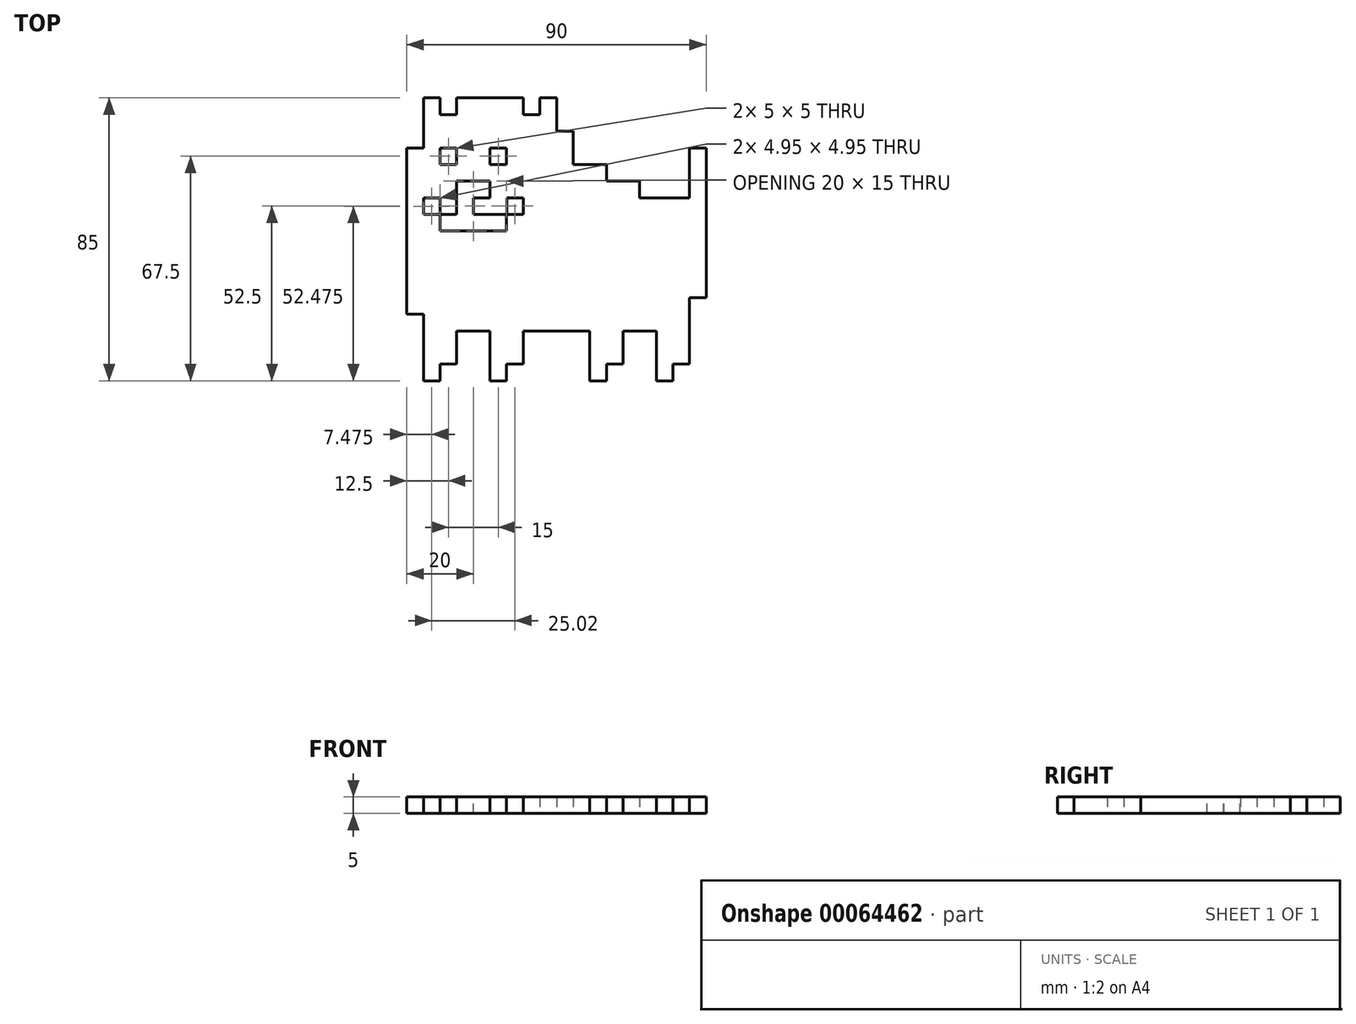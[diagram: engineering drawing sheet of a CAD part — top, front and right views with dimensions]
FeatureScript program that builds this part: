
annotation { "Feature Type Name" : "Feature", "Feature Type Description" : "" }
export const myFeature = defineFeature(function(context is Context, id is Id, definition is map)
    precondition{}
    {
        {
            var Q0;
            Q0=qCreatedBy(makeId("Top.planeOp"),FACE);
            var sketch = newSketch(context, id + "F0", { "sketchPlane" : qUnion([Q0])});
            skPoint(sketch, "E0", {"position": v(0, 25) * mm});
            skPoint(sketch, "E1", {"position": v(0, -25) * mm});
            skLineSegment(sketch, "E2", {"start": v(0, 25) * mm, "end": v(0, -25) * mm});
            skLineSegment(sketch, "E3", {"start": v(0, 25) * mm, "end": v(5, 25) * mm});
            skLineSegment(sketch, "E4", {"start": v(5, 25) * mm, "end": v(5, 40) * mm});
            skLineSegment(sketch, "E5", {"start": v(5, 40) * mm, "end": v(10, 40) * mm});
            skLineSegment(sketch, "E6", {"start": v(10, 40) * mm, "end": v(10, 35) * mm});
            skLineSegment(sketch, "E7", {"start": v(10, 35) * mm, "end": v(15, 35) * mm});
            skLineSegment(sketch, "E8", {"start": v(15, 35) * mm, "end": v(15, 40) * mm});
            skLineSegment(sketch, "E9", {"start": v(15, 40) * mm, "end": v(35, 40) * mm});
            skLineSegment(sketch, "E10", {"start": v(35, 40) * mm, "end": v(35, 35) * mm});
            skLineSegment(sketch, "E11", {"start": v(35, 35) * mm, "end": v(40, 35) * mm});
            skLineSegment(sketch, "E12", {"start": v(40, 35) * mm, "end": v(40, 40) * mm});
            skLineSegment(sketch, "E13", {"start": v(40, 40) * mm, "end": v(45, 40) * mm});
            skLineSegment(sketch, "E14", {"start": v(45, 40) * mm, "end": v(45, 30) * mm});
            skLineSegment(sketch, "E15", {"start": v(45, 30) * mm, "end": v(50, 30) * mm});
            skLineSegment(sketch, "E16", {"start": v(50, 30) * mm, "end": v(50, 20) * mm});
            skLineSegment(sketch, "E17", {"start": v(50, 20) * mm, "end": v(60, 20) * mm});
            skLineSegment(sketch, "E18", {"start": v(60, 20) * mm, "end": v(60, 15) * mm});
            skLineSegment(sketch, "E19", {"start": v(60, 15) * mm, "end": v(70, 15) * mm});
            skLineSegment(sketch, "E20", {"start": v(70, 15) * mm, "end": v(70, 10) * mm});
            skLineSegment(sketch, "E21", {"start": v(70, 10) * mm, "end": v(85, 10) * mm});
            skLineSegment(sketch, "E22", {"start": v(85, 10) * mm, "end": v(85, 25) * mm});
            skLineSegment(sketch, "E23", {"start": v(85, 25) * mm, "end": v(90, 25) * mm});
            skLineSegment(sketch, "E24", {"start": v(90, 25) * mm, "end": v(90, -20) * mm});
            skLineSegment(sketch, "E25", {"start": v(90, -20) * mm, "end": v(85, -20) * mm});
            skLineSegment(sketch, "E26", {"start": v(85, -20) * mm, "end": v(85, -40) * mm});
            skLineSegment(sketch, "E27", {"start": v(85, -40) * mm, "end": v(80, -40) * mm});
            skLineSegment(sketch, "E28", {"start": v(80, -40) * mm, "end": v(80, -45) * mm});
            skLineSegment(sketch, "E29", {"start": v(80, -45) * mm, "end": v(75, -45) * mm});
            skLineSegment(sketch, "E30", {"start": v(75, -45) * mm, "end": v(75, -30) * mm});
            skLineSegment(sketch, "E31", {"start": v(75, -30) * mm, "end": v(65, -30) * mm});
            skLineSegment(sketch, "E32", {"start": v(65, -30) * mm, "end": v(65, -40) * mm});
            skLineSegment(sketch, "E33", {"start": v(65, -40) * mm, "end": v(60, -40) * mm});
            skLineSegment(sketch, "E34", {"start": v(60, -40) * mm, "end": v(60, -45) * mm});
            skLineSegment(sketch, "E35", {"start": v(60, -45) * mm, "end": v(55, -45) * mm});
            skLineSegment(sketch, "E36", {"start": v(55, -45) * mm, "end": v(55, -30) * mm});
            skLineSegment(sketch, "E37", {"start": v(55, -30) * mm, "end": v(35, -30) * mm});
            skLineSegment(sketch, "E38", {"start": v(35, -30) * mm, "end": v(35, -40) * mm});
            skLineSegment(sketch, "E39", {"start": v(35, -40) * mm, "end": v(30, -40) * mm});
            skLineSegment(sketch, "E40", {"start": v(30, -40) * mm, "end": v(30, -45) * mm});
            skLineSegment(sketch, "E41", {"start": v(30, -45) * mm, "end": v(25, -45) * mm});
            skLineSegment(sketch, "E42", {"start": v(25, -45) * mm, "end": v(25, -30) * mm});
            skLineSegment(sketch, "E43", {"start": v(25, -30) * mm, "end": v(15, -30) * mm});
            skLineSegment(sketch, "E44", {"start": v(15, -30) * mm, "end": v(15, -40) * mm});
            skLineSegment(sketch, "E45", {"start": v(15, -40) * mm, "end": v(10, -40) * mm});
            skLineSegment(sketch, "E46", {"start": v(10, -40) * mm, "end": v(10, -45) * mm});
            skLineSegment(sketch, "E47", {"start": v(10, -45) * mm, "end": v(5, -45) * mm});
            skLineSegment(sketch, "E48", {"start": v(0, -25) * mm, "end": v(5, -25) * mm});
            skLineSegment(sketch, "E49", {"start": v(5, -45) * mm, "end": v(5, -25) * mm});
            skSolve(sketch);
        }
        {
            var Q0;
            Q0 = qSketchRegion(id + "F0", true);
            extrude(context, id + "F1", {"entities" : qUnion([Q0]), "depth" : 5 * mm});
        }
        {
            var Q0;
            Q0=makeQuery(id+"F1.opExtrude","CAP_FACE",FACE,{"disambiguationData":[OSD([sQuery(id+"F0.wireOp",EDGE,"E2"),sQuery(id+"F0.wireOp",EDGE,"E3"),sQuery(id+"F0.wireOp",EDGE,"E4"),sQuery(id+"F0.wireOp",EDGE,"E5"),sQuery(id+"F0.wireOp",EDGE,"E6"),sQuery(id+"F0.wireOp",EDGE,"E7"),sQuery(id+"F0.wireOp",EDGE,"E8"),sQuery(id+"F0.wireOp",EDGE,"E9"),sQuery(id+"F0.wireOp",EDGE,"E10"),sQuery(id+"F0.wireOp",EDGE,"E11"),sQuery(id+"F0.wireOp",EDGE,"E12"),sQuery(id+"F0.wireOp",EDGE,"E13"),sQuery(id+"F0.wireOp",EDGE,"E14"),sQuery(id+"F0.wireOp",EDGE,"E15"),sQuery(id+"F0.wireOp",EDGE,"E16"),sQuery(id+"F0.wireOp",EDGE,"E17"),sQuery(id+"F0.wireOp",EDGE,"E18"),sQuery(id+"F0.wireOp",EDGE,"E19"),sQuery(id+"F0.wireOp",EDGE,"E20"),sQuery(id+"F0.wireOp",EDGE,"E21"),sQuery(id+"F0.wireOp",EDGE,"E22"),sQuery(id+"F0.wireOp",EDGE,"E23"),sQuery(id+"F0.wireOp",EDGE,"E24"),sQuery(id+"F0.wireOp",EDGE,"E25"),sQuery(id+"F0.wireOp",EDGE,"E26"),sQuery(id+"F0.wireOp",EDGE,"E27"),sQuery(id+"F0.wireOp",EDGE,"E28"),sQuery(id+"F0.wireOp",EDGE,"E29"),sQuery(id+"F0.wireOp",EDGE,"E30"),sQuery(id+"F0.wireOp",EDGE,"E31"),sQuery(id+"F0.wireOp",EDGE,"E32"),sQuery(id+"F0.wireOp",EDGE,"E33"),sQuery(id+"F0.wireOp",EDGE,"E34"),sQuery(id+"F0.wireOp",EDGE,"E35"),sQuery(id+"F0.wireOp",EDGE,"E36"),sQuery(id+"F0.wireOp",EDGE,"E37"),sQuery(id+"F0.wireOp",EDGE,"E38"),sQuery(id+"F0.wireOp",EDGE,"E39"),sQuery(id+"F0.wireOp",EDGE,"E40"),sQuery(id+"F0.wireOp",EDGE,"E41"),sQuery(id+"F0.wireOp",EDGE,"E42"),sQuery(id+"F0.wireOp",EDGE,"E43"),sQuery(id+"F0.wireOp",EDGE,"E44"),sQuery(id+"F0.wireOp",EDGE,"E45"),sQuery(id+"F0.wireOp",EDGE,"E46"),sQuery(id+"F0.wireOp",EDGE,"E47"),sQuery(id+"F0.wireOp",EDGE,"E48"),sQuery(id+"F0.wireOp",EDGE,"E49")])],"isStart":false});
            var sketch = newSketch(context, id + "F2", { "sketchPlane" : qUnion([Q0])});
            skLineSegment(sketch, "E50.bottom", {"start": v(10, 25) * mm, "end": v(15, 25) * mm});
            skLineSegment(sketch, "E50.top", {"start": v(10, 20) * mm, "end": v(15, 20) * mm});
            skLineSegment(sketch, "E50.left", {"start": v(10, 25) * mm, "end": v(10, 20) * mm});
            skLineSegment(sketch, "E50.right", {"start": v(15, 25) * mm, "end": v(15, 20) * mm});
            skLineSegment(sketch, "E51.right", {"start": v(30, 25) * mm, "end": v(30, 20) * mm});
            skLineSegment(sketch, "E51.left", {"start": v(25, 25) * mm, "end": v(25, 20) * mm});
            skLineSegment(sketch, "E51.top", {"start": v(25, 20) * mm, "end": v(30, 20) * mm});
            skLineSegment(sketch, "E51.bottom", {"start": v(25, 25) * mm, "end": v(30, 25) * mm});
            skLineSegment(sketch, "E52.right", {"start": v(10, 10) * mm, "end": v(10, 5) * mm});
            skLineSegment(sketch, "E52.left", {"start": v(5, 10) * mm, "end": v(5, 5) * mm});
            skLineSegment(sketch, "E52.top", {"start": v(5, 5) * mm, "end": v(10, 5) * mm});
            skLineSegment(sketch, "E52.bottom", {"start": v(5, 10) * mm, "end": v(10, 10) * mm});
            skLineSegment(sketch, "E53.right", {"start": v(35, 10) * mm, "end": v(35, 5) * mm});
            skLineSegment(sketch, "E53.left", {"start": v(30, 10) * mm, "end": v(30, 5) * mm});
            skLineSegment(sketch, "E53.top", {"start": v(30, 5) * mm, "end": v(35, 5) * mm});
            skLineSegment(sketch, "E53.bottom", {"start": v(30, 10) * mm, "end": v(35, 10) * mm});
            skLineSegment(sketch, "E54.bottom", {"start": v(10, 5) * mm, "end": v(15, 5) * mm});
            skLineSegment(sketch, "E54.top", {"start": v(10, 0) * mm, "end": v(30, 0) * mm});
            skLineSegment(sketch, "E54.left", {"start": v(10, 5) * mm, "end": v(10, 0) * mm});
            skLineSegment(sketch, "E54.right", {"start": v(30, 5) * mm, "end": v(30, 0) * mm});
            skLineSegment(sketch, "E55", {"start": v(15, 5) * mm, "end": v(15, 15) * mm});
            skLineSegment(sketch, "E56", {"start": v(15, 15) * mm, "end": v(25, 15) * mm});
            skLineSegment(sketch, "E57", {"start": v(25, 15) * mm, "end": v(25, 10) * mm});
            skLineSegment(sketch, "E58", {"start": v(25, 10) * mm, "end": v(20, 10) * mm});
            skLineSegment(sketch, "E59", {"start": v(20, 10) * mm, "end": v(20, 5) * mm});
            skLineSegment(sketch, "E60.trimOffspring", {"start": v(20, 5) * mm, "end": v(30, 5) * mm});
            skSolve(sketch);
        }
        {
            var Q0;
            Q0=makeQuery(id+"F2.imprint","IMPRINT",FACE,{"disambiguationData":[TD([[makeQuery(id+"F2.imprint","IMPRINT",EDGE,{"derivedFrom":sQuery(id+"F2.wireOp",EDGE,"E54.bottom")}),-1.0]])]});
            extrude(context, id + "F3", {"entities" : qUnion([Q0]), "operationType" : NewBodyOperationType.REMOVE, "oppositeDirection" : true, "depth" : 25 * mm});
        }
        {
            var Q0;
            Q0=makeQuery(id+"F2.imprint","IMPRINT",FACE,{"disambiguationData":[TD([[makeQuery(id+"F2.imprint","IMPRINT",EDGE,{"derivedFrom":sQuery(id+"F2.wireOp",EDGE,"E50.bottom")}),1.0]])]});
            var sketch = newSketch(context, id + "F4", { "sketchPlane" : qUnion([Q0])});
            skLineSegment(sketch, "E61.bottom", {"start": v(10, 25) * mm, "end": v(15, 25) * mm});
            skLineSegment(sketch, "E61.top", {"start": v(10, 20) * mm, "end": v(15, 20) * mm});
            skLineSegment(sketch, "E61.left", {"start": v(10, 25) * mm, "end": v(10, 20) * mm});
            skLineSegment(sketch, "E61.right", {"start": v(15, 25) * mm, "end": v(15, 20) * mm});
            skSolve(sketch);
        }
        {
            var Q0;
            Q0 = qSketchRegion(id + "F4", true);
            extrude(context, id + "F5", {"entities" : qUnion([Q0]), "operationType" : NewBodyOperationType.REMOVE, "oppositeDirection" : true, "depth" : 25 * mm});
        }
        {
            var Q0;
            Q0=makeQuery(id+"F2.imprint","IMPRINT",FACE,{"disambiguationData":[TD([[makeQuery(id+"F2.imprint","IMPRINT",EDGE,{"derivedFrom":sQuery(id+"F2.wireOp",EDGE,"E50.bottom")}),1.0]])]});
            var sketch = newSketch(context, id + "F6", { "sketchPlane" : qUnion([Q0])});
            skLineSegment(sketch, "E62.bottom", {"start": v(25, 25) * mm, "end": v(30, 25) * mm});
            skLineSegment(sketch, "E62.top", {"start": v(25, 20) * mm, "end": v(30, 20) * mm});
            skLineSegment(sketch, "E62.left", {"start": v(25, 25) * mm, "end": v(25, 20) * mm});
            skLineSegment(sketch, "E62.right", {"start": v(30, 25) * mm, "end": v(30, 20) * mm});
            skSolve(sketch);
        }
        {
            var Q0;
            Q0 = qSketchRegion(id + "F6", true);
            extrude(context, id + "F7", {"entities" : qUnion([Q0]), "operationType" : NewBodyOperationType.REMOVE, "oppositeDirection" : true, "depth" : 25 * mm});
        }
        {
            var Q0;
            Q0=makeQuery(id+"F2.imprint","IMPRINT",FACE,{"disambiguationData":[TD([[makeQuery(id+"F2.imprint","IMPRINT",EDGE,{"derivedFrom":sQuery(id+"F2.wireOp",EDGE,"E50.bottom")}),1.0]])]});
            var sketch = newSketch(context, id + "F8", { "sketchPlane" : qUnion([Q0])});
            skLineSegment(sketch, "E63.bottom", {"start": v(5, 9.95) * mm, "end": v(9.95, 9.95) * mm});
            skLineSegment(sketch, "E63.top", {"start": v(5, 5) * mm, "end": v(9.95, 5) * mm});
            skLineSegment(sketch, "E63.left", {"start": v(5, 9.95) * mm, "end": v(5, 5) * mm});
            skLineSegment(sketch, "E63.right", {"start": v(9.95, 9.95) * mm, "end": v(9.95, 5) * mm});
            skSolve(sketch);
        }
        {
            var Q0;
            Q0 = qSketchRegion(id + "F8", true);
            extrude(context, id + "F9", {"entities" : qUnion([Q0]), "operationType" : NewBodyOperationType.REMOVE, "oppositeDirection" : true, "depth" : 25 * mm});
        }
        {
            var Q0;
            Q0=makeQuery(id+"F4.imprint","IMPRINT",FACE,{"disambiguationData":[TD([[makeQuery(id+"F4.imprint","IMPRINT",EDGE,{"derivedFrom":sQuery(id+"F4.wireOp",EDGE,"E61.bottom")}),1.0]])]});
            var sketch = newSketch(context, id + "F10", { "sketchPlane" : qUnion([Q0])});
            skLineSegment(sketch, "E64.bottom", {"start": v(30.02, 10) * mm, "end": v(34.97, 10) * mm});
            skLineSegment(sketch, "E64.top", {"start": v(30.02, 5.05) * mm, "end": v(34.97, 5.05) * mm});
            skLineSegment(sketch, "E64.left", {"start": v(30.02, 10) * mm, "end": v(30.02, 5.05) * mm});
            skLineSegment(sketch, "E64.right", {"start": v(34.97, 10) * mm, "end": v(34.97, 5.05) * mm});
            skSolve(sketch);
        }
        {
            var Q0;
            Q0 = qSketchRegion(id + "F10", true);
            extrude(context, id + "F11", {"entities" : qUnion([Q0]), "operationType" : NewBodyOperationType.REMOVE, "oppositeDirection" : true, "depth" : 25 * mm});
        }
    });
